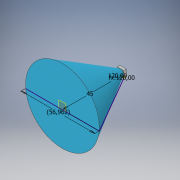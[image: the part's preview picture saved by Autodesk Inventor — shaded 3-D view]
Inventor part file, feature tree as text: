
AUTODESK INVENTOR PART (.ipt)
format: ipt  version: 2019 (Build 230136000, 136)  size: 128,512 bytes
history: native  units: mm
features: sketch x4, extrude x1, plane x1, loft x1, projected_geometry x1
ambient origin geometry x8: Origin, YZ Plane, XZ Plane, XY Plane, X Axis, Y Axis, Z Axis, Center Point
bodies: Solid1 (feature_tree)
feature tree (8):
  extrude  "Extrusion1"  Depth=5.0mm
  sketch  "Sketch2"  dims[d2=4.5mm d3=2.0mm d4=0.0mm]
  sketch  "Sketch3"  dims[d5=120.0deg]
  plane  "Work Plane1"
  loft  "Loft1"
  sketch  "Sketch1"  dims[d0=5.0mm d1=5.0mm]
  projected_geometry  "Projected Loop1"
  sketch  "Sketch4"  dims[d6=120.0deg d7=45.0mm d8=45.0mm d9=56.961524mm d10=57.0mm d11=0.0mm d12=90.0deg d13=0.0mm d14=90.0deg]
